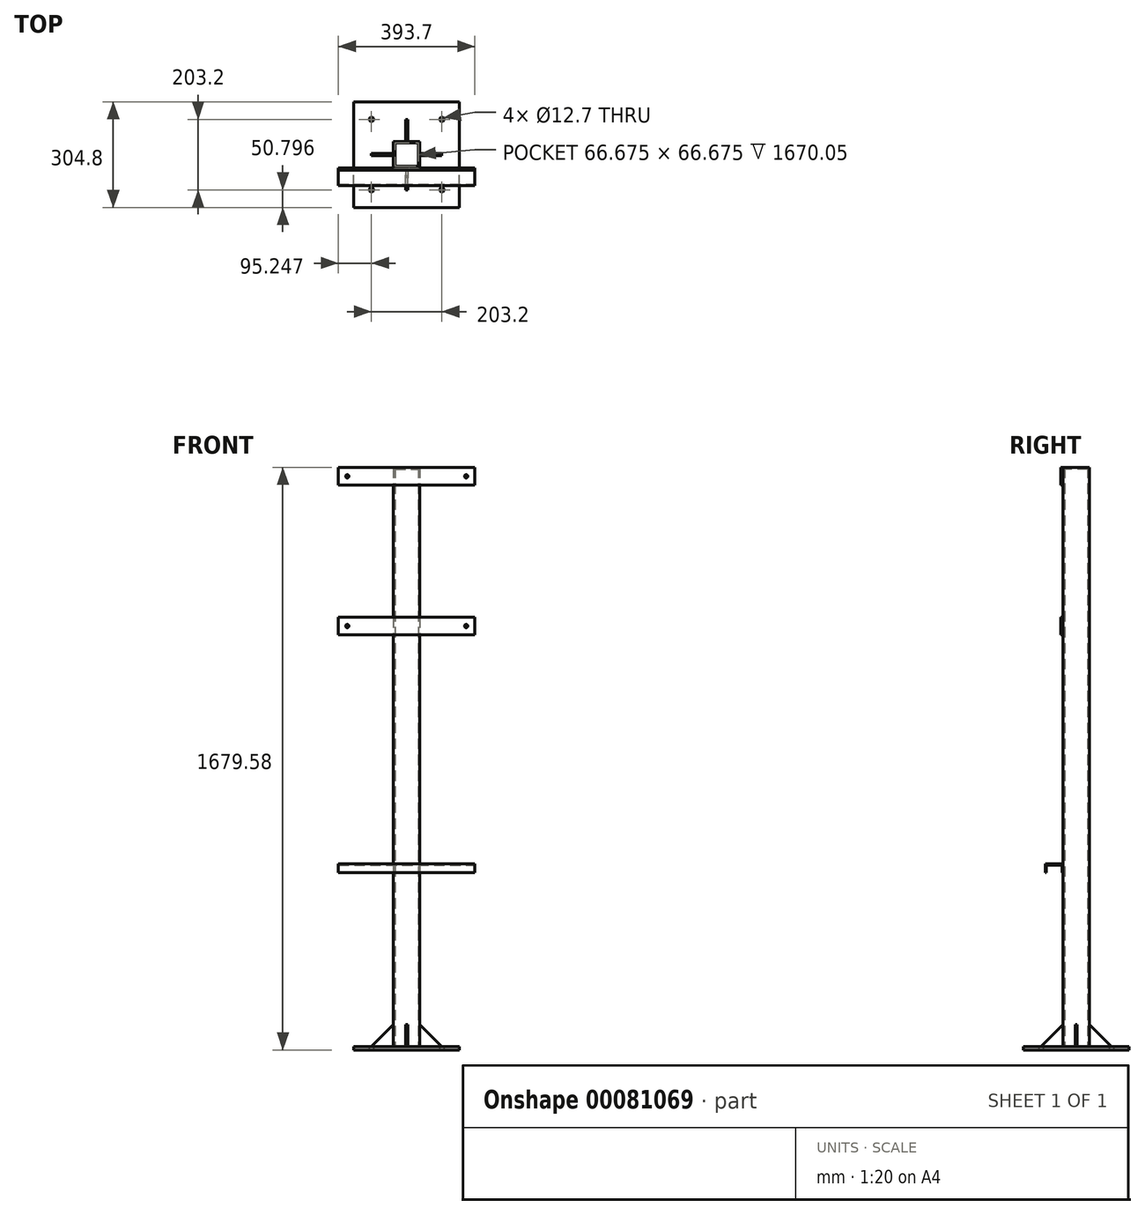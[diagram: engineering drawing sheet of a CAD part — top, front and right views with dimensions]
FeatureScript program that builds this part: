
annotation { "Feature Type Name" : "Feature", "Feature Type Description" : "" }
export const myFeature = defineFeature(function(context is Context, id is Id, definition is map)
    precondition{}
    {
        {
            var Q0;
            Q0=qCreatedBy(makeId("Top.planeOp"),FACE);
            var sketch = newSketch(context, id + "F0", { "sketchPlane" : qUnion([Q0])});
            skLineSegment(sketch, "E0.bottom", {"start": v(-38.12, 37.72) * mm, "end": v(38.08, 37.72) * mm});
            skLineSegment(sketch, "E0.top", {"start": v(-38.12, -38.48) * mm, "end": v(38.08, -38.48) * mm});
            skLineSegment(sketch, "E0.left", {"start": v(-38.12, 37.72) * mm, "end": v(-38.12, -38.48) * mm});
            skLineSegment(sketch, "E0.right", {"start": v(38.08, 37.72) * mm, "end": v(38.08, -38.48) * mm});
            skLineSegment(sketch, "E1.0", {"start": v(-33.36, 32.95) * mm, "end": v(-33.36, -33.72) * mm});
            skLineSegment(sketch, "E1.1", {"start": v(-33.36, 32.95) * mm, "end": v(33.31, 32.95) * mm});
            skLineSegment(sketch, "E1.2", {"start": v(33.31, 32.95) * mm, "end": v(33.31, -33.72) * mm});
            skLineSegment(sketch, "E1.3", {"start": v(-33.36, -33.72) * mm, "end": v(33.31, -33.72) * mm});
            skSolve(sketch);
        }
        {
            var Q0;
            Q0=makeQuery(id+"F0.imprint","IMPRINT",FACE,{"disambiguationData":[TD([[makeQuery(id+"F0.imprint","IMPRINT",EDGE,{"derivedFrom":sQuery(id+"F0.wireOp",EDGE,"E0.bottom")}),-1.0]])]});
            extrude(context, id + "F1", {"entities" : qUnion([Q0]), "depth" : 2133.6 * mm});
        }
        {
            var Q0;
            Q0=makeQuery(id+"F1.opExtrude","CAP_FACE",FACE,{"disambiguationData":[OSD([sQuery(id+"F0.wireOp",EDGE,"E0.bottom"),sQuery(id+"F0.wireOp",EDGE,"E0.top"),sQuery(id+"F0.wireOp",EDGE,"E0.left"),sQuery(id+"F0.wireOp",EDGE,"E0.right"),sQuery(id+"F0.wireOp",EDGE,"E1.0"),sQuery(id+"F0.wireOp",EDGE,"E1.1"),sQuery(id+"F0.wireOp",EDGE,"E1.2"),sQuery(id+"F0.wireOp",EDGE,"E1.3")])],"isStart":false});
            var sketch = newSketch(context, id + "F2", { "sketchPlane" : qUnion([Q0])});
            skSolve(sketch);
        }
        {
            var Q0;
            Q0=makeQuery(id+"F2.imprint","IMPRINT",FACE,{"disambiguationData":[TD([[makeQuery(id+"F2.imprint","IMPRINT",EDGE,{"derivedFrom":makeQuery(id+"F1.opExtrude","CAP_EDGE",EDGE,{"disambiguationData":[OSD([sQuery(id+"F0.wireOp",EDGE,"E1.0")])],"isStart":false})}),1.0]])]});
            var sketch = newSketch(context, id + "F3", { "sketchPlane" : qUnion([Q0])});
            skSolve(sketch);
        }
        {
            var Q0;
            Q0=qSketchRegion(id+"F3",true);
            var Q1;
            Q1=makeQuery(id+"F2.imprint","IMPRINT",FACE,{"disambiguationData":[TD([[makeQuery(id+"F2.imprint","IMPRINT",EDGE,{"derivedFrom":makeQuery(id+"F1.opExtrude","CAP_EDGE",EDGE,{"disambiguationData":[OSD([sQuery(id+"F0.wireOp",EDGE,"E1.0")])],"isStart":false})}),1.0]])]});
            extrude(context, id + "F4", {"entities" : qUnion([Q0, Q1]), "oppositeDirection" : true, "depth" : 4.76 * mm});
        }
        {
            var Q0;
            Q0=makeQuery(id+"F1.opExtrude","SWEPT_FACE",FACE,{"disambiguationData":[OSD([sQuery(id+"F0.wireOp",EDGE,"E0.top")])]});
            var sketch = newSketch(context, id + "F5", { "sketchPlane" : qUnion([Q0])});
            skLineSegment(sketch, "E2", {"start": v(-38.12, 2133.6) * mm, "end": v(-196.87, 2133.6) * mm});
            skLineSegment(sketch, "E3", {"start": v(-196.87, 2133.6) * mm, "end": v(-196.87, 2082.8) * mm});
            skLineSegment(sketch, "E4", {"start": v(-196.87, 2082.8) * mm, "end": v(196.83, 2082.8) * mm});
            skLineSegment(sketch, "E5", {"start": v(196.83, 2082.8) * mm, "end": v(196.83, 2133.6) * mm});
            skLineSegment(sketch, "E6", {"start": v(-38.12, 2133.6) * mm, "end": v(38.08, 2133.6) * mm});
            skLineSegment(sketch, "E7", {"start": v(38.08, 2133.6) * mm, "end": v(196.83, 2133.6) * mm});
            skCircle(sketch, "E8", {"center": v(-171.47, 2108.2) * mm, "radius": 4.76 * mm});
            skCircle(sketch, "E9", {"center": v(171.43, 2108.2) * mm, "radius": 4.76 * mm});
            skLineSegment(sketch, "E10", {"start": v(-196.87, 1701.8) * mm, "end": v(-38.12, 1701.8) * mm});
            skLineSegment(sketch, "E11", {"start": v(-38.12, 1701.8) * mm, "end": v(38.08, 1701.8) * mm});
            skLineSegment(sketch, "E12", {"start": v(38.08, 1701.8) * mm, "end": v(196.83, 1701.8) * mm});
            skLineSegment(sketch, "E13", {"start": v(196.83, 1701.8) * mm, "end": v(196.83, 1650.99) * mm});
            skLineSegment(sketch, "E14", {"start": v(196.83, 1650.99) * mm, "end": v(-196.87, 1650.99) * mm});
            skLineSegment(sketch, "E15", {"start": v(-196.87, 1650.99) * mm, "end": v(-196.87, 1701.8) * mm});
            skCircle(sketch, "E16", {"center": v(171.43, 1676.4) * mm, "radius": 4.76 * mm});
            skCircle(sketch, "E17", {"center": v(-171.47, 1676.4) * mm, "radius": 4.76 * mm});
            skSolve(sketch);
        }
        {
            var Q0;
            Q0=makeQuery(id+"F1.opExtrude","CAP_FACE",FACE,{"disambiguationData":[OSD([sQuery(id+"F0.wireOp",EDGE,"E0.bottom"),sQuery(id+"F0.wireOp",EDGE,"E0.top"),sQuery(id+"F0.wireOp",EDGE,"E0.left"),sQuery(id+"F0.wireOp",EDGE,"E0.right"),sQuery(id+"F0.wireOp",EDGE,"E1.0"),sQuery(id+"F0.wireOp",EDGE,"E1.1"),sQuery(id+"F0.wireOp",EDGE,"E1.2"),sQuery(id+"F0.wireOp",EDGE,"E1.3")])],"isStart":true});
            extrude(context, id + "F6", {"entities" : qUnion([Q0]), "operationType" : NewBodyOperationType.REMOVE, "oppositeDirection" : true, "depth" : 457.2 * mm});
        }
        {
            var Q0;
            Q0=makeQuery(id+"F6.boolean.opBoolean","COPY",FACE,{"derivedFrom":makeQuery(id+"F6.opExtrude","CAP_FACE",FACE,{"disambiguationData":[OSD([sQuery(id+"F0.wireOp",EDGE,"E0.bottom"),sQuery(id+"F0.wireOp",EDGE,"E0.top"),sQuery(id+"F0.wireOp",EDGE,"E0.left"),sQuery(id+"F0.wireOp",EDGE,"E0.right"),sQuery(id+"F0.wireOp",EDGE,"E1.0"),sQuery(id+"F0.wireOp",EDGE,"E1.1"),sQuery(id+"F0.wireOp",EDGE,"E1.2"),sQuery(id+"F0.wireOp",EDGE,"E1.3")])],"isStart":false})});
            cPlane(context, id + "F7", {"entities" : qUnion([Q0]), "cplaneType" : CPlaneType.OFFSET, "offset" : 0 * mm, "width" : 152.4 * mm, "height" : 152.4 * mm});
        }
        {
            var Q0;
            Q0=qCreatedBy(id+"F7.planeOp",FACE);
            var sketch = newSketch(context, id + "F8", { "sketchPlane" : qUnion([Q0])});
            skLineSegment(sketch, "E18.bottom", {"start": v(-152.42, 152.78) * mm, "end": v(152.38, 152.78) * mm});
            skLineSegment(sketch, "E18.top", {"start": v(-152.42, -152.02) * mm, "end": v(152.38, -152.02) * mm});
            skLineSegment(sketch, "E18.left", {"start": v(-152.42, 152.78) * mm, "end": v(-152.42, -152.02) * mm});
            skLineSegment(sketch, "E18.right", {"start": v(152.38, 152.78) * mm, "end": v(152.38, -152.02) * mm});
            skCircle(sketch, "E19", {"center": v(-101.62, 101.98) * mm, "radius": 6.35 * mm});
            skCircle(sketch, "E20", {"center": v(101.58, 101.98) * mm, "radius": 6.35 * mm});
            skCircle(sketch, "E21", {"center": v(-101.62, -101.22) * mm, "radius": 6.35 * mm});
            skCircle(sketch, "E22", {"center": v(101.58, -101.22) * mm, "radius": 6.35 * mm});
            skSolve(sketch);
        }
        {
            var Q0;
            Q0=makeQuery(id+"F8.imprint","IMPRINT",FACE,{"disambiguationData":[TD([[makeQuery(id+"F8.imprint","IMPRINT",EDGE,{"derivedFrom":sQuery(id+"F8.wireOp",EDGE,"E18.bottom")}),-1.0]])]});
            extrude(context, id + "F9", {"entities" : qUnion([Q0]), "operationType" : NewBodyOperationType.ADD, "oppositeDirection" : true, "depth" : 6.35 * mm});
        }
        {
            var Q0;
            {var subQ0=sQuery(id+"F5.wireOp",EDGE,"SzxpJmgs-wZaf-tbDt-Z4eK-Ztco54eoQ7zW");var subQ3=sQuery(id+"F0.wireOp",EDGE,"E0.top");Q0=makeQuery(id+"FTbxsVL5rwinNAR_2.boolean.opBoolean","SPLIT",FACE,{"disambiguationData":[TD([makeQuery(id+"FTbxsVL5rwinNAR_2.opExtrude","SWEPT_FACE",FACE,{"disambiguationData":[OSD([subQ0])]})])],"derivedFrom":makeQuery(id+"F1.opExtrude","SWEPT_FACE",FACE,{"disambiguationData":[OSD([subQ3])]})});}
            cPlane(context, id + "F10", {"entities" : qUnion([Q0]), "cplaneType" : CPlaneType.OFFSET, "offset" : 38.1 * mm, "oppositeDirection" : true, "width" : 152.4 * mm, "height" : 152.4 * mm});
        }
        {
            var Q0;
            Q0=qCreatedBy(id+"F10.planeOp",FACE);
            var sketch = newSketch(context, id + "F11", { "sketchPlane" : qUnion([Q0])});
            skLineSegment(sketch, "E23", {"start": v(38.08, 527.05) * mm, "end": v(101.58, 463.55) * mm});
            skLineSegment(sketch, "E24", {"start": v(101.58, 463.55) * mm, "end": v(38.08, 463.55) * mm});
            skLineSegment(sketch, "E25", {"start": v(38.08, 463.55) * mm, "end": v(38.08, 527.05) * mm});
            skLineSegment(sketch, "E26", {"start": v(-38.12, 527.05) * mm, "end": v(-38.12, 463.55) * mm});
            skLineSegment(sketch, "E27", {"start": v(-38.12, 463.55) * mm, "end": v(-101.62, 463.55) * mm});
            skLineSegment(sketch, "E28", {"start": v(-101.62, 463.55) * mm, "end": v(-38.12, 527.05) * mm});
            skSolve(sketch);
        }
        {
            var Q0;
            Q0 = qSketchRegion(id + "F8", true);
            extrude(context, id + "F12", {"entities" : qUnion([Q0]), "operationType" : NewBodyOperationType.ADD, "depth" : 3.17 * mm});
        }
        {
            var Q0;
            Q0 = qSketchRegion(id + "F11", true);
            var Q1;
            Q1=makeQuery(id+"F12.opExtrude","CAP_FACE",FACE,{"disambiguationData":[OSD([sQuery(id+"F11.wireOp",EDGE,"E23"),sQuery(id+"F11.wireOp",EDGE,"E24"),sQuery(id+"F11.wireOp",EDGE,"E25")])],"isStart":false});
            extrude(context, id + "F13", {"entities" : qUnion([Q0, Q1]), "operationType" : NewBodyOperationType.ADD, "oppositeDirection" : true, "depth" : 3.17 * mm});
        }
        {
            var Q0;
            Q0=qCreatedBy(makeId("Right.planeOp"),FACE);
            var sketch = newSketch(context, id + "F14", { "sketchPlane" : qUnion([Q0])});
            skLineSegment(sketch, "E29", {"start": v(37.72, 527.05) * mm, "end": v(101.22, 463.55) * mm});
            skLineSegment(sketch, "E30", {"start": v(101.22, 463.55) * mm, "end": v(37.72, 463.55) * mm});
            skLineSegment(sketch, "E31", {"start": v(37.72, 463.55) * mm, "end": v(37.72, 527.05) * mm});
            skLineSegment(sketch, "E32", {"start": v(-38.48, 527.05) * mm, "end": v(-38.48, 463.55) * mm});
            skLineSegment(sketch, "E33", {"start": v(-38.48, 463.55) * mm, "end": v(-101.98, 463.55) * mm});
            skLineSegment(sketch, "E34", {"start": v(-101.98, 463.55) * mm, "end": v(-38.48, 527.05) * mm});
            skSolve(sketch);
        }
        {
            var Q0;
            Q0 = qSketchRegion(id + "F14", true);
            extrude(context, id + "F15", {"entities" : qUnion([Q0]), "operationType" : NewBodyOperationType.ADD, "depth" : 3.17 * mm});
        }
        {
            var Q0;
            Q0 = qSketchRegion(id + "F14", true);
            extrude(context, id + "F16", {"entities" : qUnion([Q0]), "operationType" : NewBodyOperationType.ADD, "oppositeDirection" : true, "depth" : 3.17 * mm});
        }
        {
            var Q0;
            Q0 = qSketchRegion(id + "F11", true);
            var Q1;
            Q1=makeQuery(id+"F13.opExtrude","CAP_FACE",FACE,{"disambiguationData":[OSD([sQuery(id+"F11.wireOp",EDGE,"E23"),sQuery(id+"F11.wireOp",EDGE,"E24"),sQuery(id+"F11.wireOp",EDGE,"E25")])],"isStart":true});
            extrude(context, id + "F17", {"entities" : qUnion([Q0, Q1]), "operationType" : NewBodyOperationType.ADD, "depth" : 3.17 * mm});
        }
        {
            var Q0;
            {var subQ1=sQuery(id+"F5.wireOp",EDGE,"E10");Q0=makeQuery(id+"F5.imprint","IMPRINT",FACE,{"disambiguationData":[TD([[makeQuery(id+"F5.imprint","IMPRINT",EDGE,{"derivedFrom":subQ1}),-1.0]])]});}
            var Q1;
            {var subQ4=sQuery(id+"F5.wireOp",EDGE,"E12");Q1=makeQuery(id+"F5.imprint","IMPRINT",FACE,{"disambiguationData":[TD([[makeQuery(id+"F5.imprint","IMPRINT",EDGE,{"derivedFrom":subQ4}),-1.0]])]});}
            var Q2;
            {var subQ0=sQuery(id+"F5.wireOp",EDGE,"E11");Q2=makeQuery(id+"F5.imprint","IMPRINT",FACE,{"disambiguationData":[TD([[makeQuery(id+"F5.imprint","IMPRINT",EDGE,{"derivedFrom":subQ0}),-1.0]])]});}
            var Q3;
            {var subQ4=sQuery(id+"F5.wireOp",EDGE,"E2");Q3=makeQuery(id+"F5.imprint","IMPRINT",FACE,{"disambiguationData":[TD([[makeQuery(id+"F5.imprint","IMPRINT",EDGE,{"derivedFrom":subQ4}),1.0]])]});}
            var Q4;
            {var subQ6=sQuery(id+"F5.wireOp",EDGE,"E6");Q4=makeQuery(id+"F5.imprint","IMPRINT",FACE,{"disambiguationData":[TD([[makeQuery(id+"F5.imprint","IMPRINT",EDGE,{"derivedFrom":subQ6}),-1.0]])]});}
            var Q5;
            {var subQ1=sQuery(id+"F5.wireOp",EDGE,"E5");Q5=makeQuery(id+"F5.imprint","IMPRINT",FACE,{"disambiguationData":[TD([[makeQuery(id+"F5.imprint","IMPRINT",EDGE,{"derivedFrom":subQ1}),1.0]])]});}
            extrude(context, id + "F18", {"entities" : qUnion([Q0, Q1, Q2, Q3, Q4, Q5]), "operationType" : NewBodyOperationType.ADD, "depth" : 6.35 * mm});
        }
        {
            var Q0;
            {var subQ0=sQuery(id+"F14.wireOp",EDGE,"E34");Q0=makeQuery(id+"F18.boolean.opBoolean","SPLIT",FACE,{"disambiguationData":[TD([makeQuery(id+"F15.opExtrude","SWEPT_FACE",FACE,{"disambiguationData":[OSD([subQ0])]})])],"derivedFrom":makeQuery(id+"F1.opExtrude","SWEPT_FACE",FACE,{"disambiguationData":[OSD([sQuery(id+"F0.wireOp",EDGE,"E0.top")])]})});}
            var sketch = newSketch(context, id + "F19", { "sketchPlane" : qUnion([Q0])});
            skLineSegment(sketch, "E35", {"start": v(38.08, 990.6) * mm, "end": v(196.83, 990.6) * mm});
            skLineSegment(sketch, "E36", {"start": v(196.83, 990.6) * mm, "end": v(196.83, 965.2) * mm});
            skLineSegment(sketch, "E37", {"start": v(196.83, 965.2) * mm, "end": v(-196.87, 965.2) * mm});
            skLineSegment(sketch, "E38", {"start": v(-196.87, 965.2) * mm, "end": v(-196.87, 990.6) * mm});
            skLineSegment(sketch, "E39", {"start": v(-196.87, 990.6) * mm, "end": v(-38.12, 990.6) * mm});
            skLineSegment(sketch, "E40", {"start": v(-38.12, 990.6) * mm, "end": v(38.08, 990.6) * mm});
            skSolve(sketch);
        }
        {
            var Q0;
            {var subQ0=sQuery(id+"F19.wireOp",EDGE,"E35");Q0=makeQuery(id+"F19.imprint","IMPRINT",FACE,{"disambiguationData":[TD([[makeQuery(id+"F19.imprint","IMPRINT",EDGE,{"derivedFrom":subQ0}),-1.0]])]});}
            var Q1;
            {var subQ13=sQuery(id+"F19.wireOp",EDGE,"E40");Q1=makeQuery(id+"F19.imprint","IMPRINT",FACE,{"disambiguationData":[TD([[makeQuery(id+"F19.imprint","IMPRINT",EDGE,{"derivedFrom":subQ13}),-1.0]])]});}
            var Q2;
            {var subQ0=sQuery(id+"F19.wireOp",EDGE,"E38");Q2=makeQuery(id+"F19.imprint","IMPRINT",FACE,{"disambiguationData":[TD([[makeQuery(id+"F19.imprint","IMPRINT",EDGE,{"derivedFrom":subQ0}),-1.0]])]});}
            extrude(context, id + "F20", {"entities" : qUnion([Q0, Q1, Q2]), "operationType" : NewBodyOperationType.ADD, "depth" : 50.8 * mm});
        }
        {
            var Q0;
            Q0=makeQuery(id+"F20.opExtrude","SWEPT_FACE",FACE,{"disambiguationData":[OSD([sQuery(id+"F19.wireOp",EDGE,"E36")])]});
            var sketch = newSketch(context, id + "F21", { "sketchPlane" : qUnion([Q0])});
            skLineSegment(sketch, "E41", {"start": v(-89.28, 965.2) * mm, "end": v(-86.1, 965.2) * mm});
            skLineSegment(sketch, "E42", {"start": v(-86.1, 965.2) * mm, "end": v(-86.1, 987.42) * mm});
            skLineSegment(sketch, "E43", {"start": v(-86.1, 987.42) * mm, "end": v(-41.66, 987.42) * mm});
            skLineSegment(sketch, "E44", {"start": v(-41.66, 987.42) * mm, "end": v(-41.66, 965.2) * mm});
            skLineSegment(sketch, "E45", {"start": v(-41.66, 965.2) * mm, "end": v(-38.48, 965.2) * mm});
            skSolve(sketch);
        }
        {
            var Q0;
            {var subQ0=sQuery(id+"F21.wireOp",EDGE,"E42");Q0=makeQuery(id+"F21.imprint","IMPRINT",FACE,{"disambiguationData":[TD([[makeQuery(id+"F21.imprint","IMPRINT",EDGE,{"derivedFrom":subQ0}),-1.0]])]});}
            extrude(context, id + "F22", {"entities" : qUnion([Q0]), "operationType" : NewBodyOperationType.REMOVE, "oppositeDirection" : true, "depth" : 508 * mm});
        }
    });
